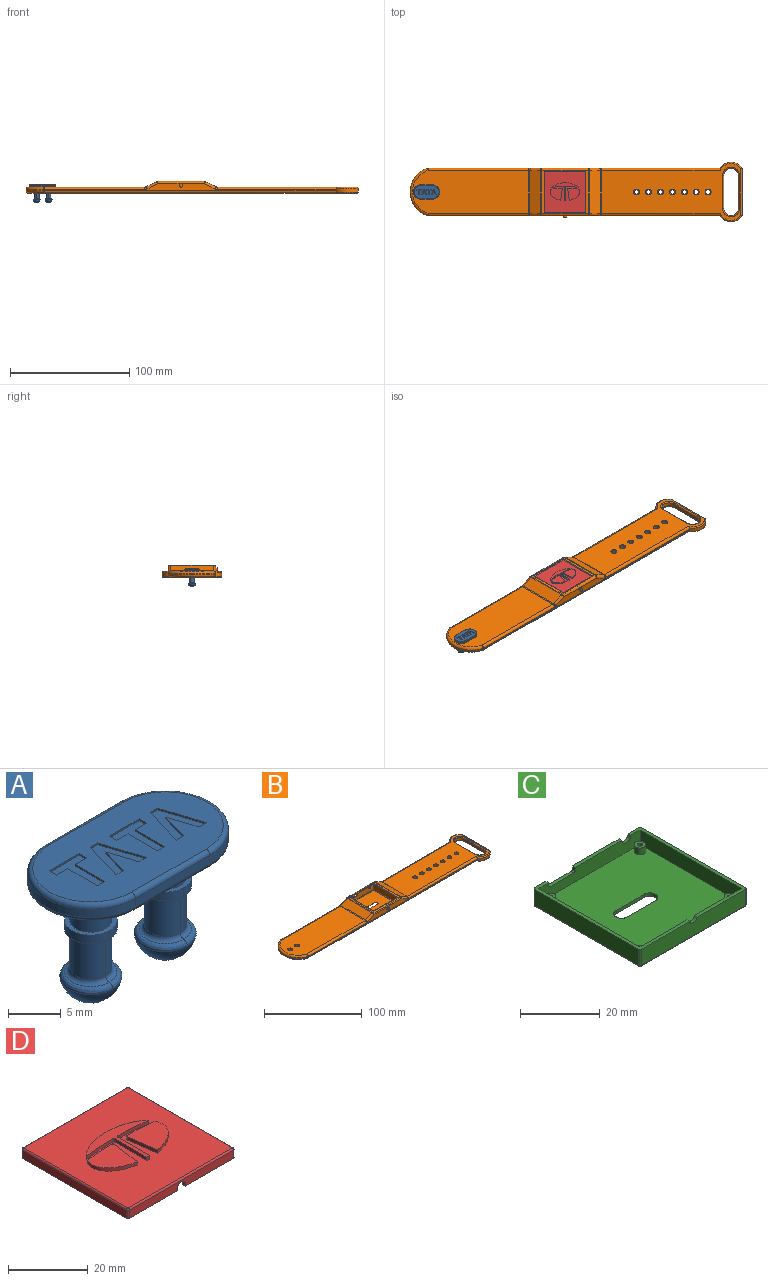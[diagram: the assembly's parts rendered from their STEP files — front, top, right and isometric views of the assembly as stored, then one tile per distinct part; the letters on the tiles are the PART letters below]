
ASSEMBLY  parts=4 mates=3
PART A: 73 faces, bbox 23x13x15 mm
  f0: plane 21x11mm, normal (0,0,1), area 171.1mm2, adj f16,f17,f18,f19,f38,f39,f40,f41
  f1: cylinder r=2.5mm len=5mm, axis (0,0,1), area 7.9mm2, adj f14,f15,f28
  f2: cylinder r=2mm len=4.5mm, axis (0,0,1), area 28.4mm2, adj f12,f27,f32
  f3: cylinder r=2mm len=4.5mm, axis (0,0,1), area 28.4mm2, adj f14,f25,f30
  f4: plane 10x1mm, normal (0,1,0), area 10mm2, adj f5,f7,f16,f20
  f5: cylinder r=6mm len=12mm, axis (0,0,1), area 18.8mm2, adj f4,f6,f17,f21
  f6: plane 10x1mm, normal (0,-1,0), area 10mm2, adj f5,f7,f19,f23
  f7: cylinder r=6mm len=12mm, axis (0,0,1), area 18.8mm2, adj f4,f6,f18,f22
  f8: plane 21x11mm, normal (0,0,-1), area 179.9mm2, adj f9,f10,f20,f21,f22,f23
  f9: cylinder r=2mm len=4mm, axis (0,0,1), area 50.3mm2, adj f8,f13
  f10: cylinder r=2mm len=4mm, axis (0,0,1), area 50.3mm2, adj f8,f15
  f11: cylinder r=2.5mm len=5mm, axis (0,0,1), area 7.9mm2, adj f12,f13,f29
  f12: plane 5.02x5mm, normal (0,0,-1), area 7mm2, adj f2,f11,f27,f29
  f13: plane 5.02x5mm, normal (0,0,1), area 7.1mm2, adj f9,f11,f29
  f14: plane 5.02x5mm, normal (0,0,-1), area 7mm2, adj f1,f3,f25,f28
  f15: plane 5.02x5mm, normal (0,0,1), area 7.1mm2, adj f1,f10,f28
  f16: cylinder r=0.5mm len=10mm, axis (-1,0,0), area 7.9mm2, adj f0,f4,f17,f18
  f17: torus R=5.5mm, axis (0,0,1), area 14.4mm2, adj f0,f5,f16,f19
  f18: torus R=5.5mm, axis (0,0,1), area 14.4mm2, adj f0,f7,f16,f19
  f19: cylinder r=0.5mm len=10mm, axis (1,0,0), area 7.9mm2, adj f0,f6,f17,f18
  f20: cylinder r=0.5mm len=10mm, axis (1,0,0), area 7.9mm2, adj f4,f8,f21,f22
  f21: torus R=5.5mm, axis (0,0,1), area 14.4mm2, adj f5,f8,f20,f23
  f22: torus R=5.5mm, axis (0,0,1), area 14.4mm2, adj f7,f8,f20,f23
  f23: cylinder r=0.5mm len=10mm, axis (-1,0,0), area 7.9mm2, adj f6,f8,f21,f22
  f24: sphere r=3mm, area 0mm2, adj f36,f37
  f25: cylinder r=2mm len=4.5mm, axis (0,0,1), area 28.4mm2, adj f3,f14,f31
  f26: sphere r=3mm, area 113.1mm2, adj f34,f35
  f27: cylinder r=2mm len=4.5mm, axis (0,0,1), area 28.4mm2, adj f2,f12,f33
  f28: cylinder r=2.5mm len=5mm, axis (0,0,1), area 7.9mm2, adj f1,f14,f15
  f29: cylinder r=2.5mm len=5mm, axis (0,0,1), area 7.9mm2, adj f11,f12,f13
  f30: torus R=2.5mm, axis (0,0,1), area 5.1mm2, adj f3,f31,f37
  f31: torus R=2.5mm, axis (0,0,1), area 5.2mm2, adj f25,f30,f36
  f32: torus R=2.5mm, axis (0,0,1), area 5.2mm2, adj f2,f33,f34
  f33: torus R=2.5mm, axis (0,0,1), area 5.1mm2, adj f27,f32,f35
  f34: bspline ~6.12x3.71mm, area 7.6mm2, adj f26,f32,f35
  f35: bspline ~5.89x2.93mm, area 7.5mm2, adj f26,f33,f34
  f36: bspline ~6.12x3.71mm, area 7.6mm2, adj f24,f31,f37
  f37: bspline ~5.89x2.93mm, area 7.5mm2, adj f24,f30,f36
  f38: plane 3.96x0.2mm, normal (-1,0,0), area 0.8mm2, adj f0,f39,f45,f46
  f39: plane 1.5x0.2mm, normal (0,1,0), area 0.3mm2, adj f0,f38,f40,f46
  f40: plane 1x0.2mm, normal (-1,0,0), area 0.2mm2, adj f0,f39,f41,f46
  f41: plane 4x0.2mm, normal (0,-1,0), area 0.8mm2, adj f0,f40,f42,f46
  f42: plane 1x0.2mm, normal (1,0,0), area 0.2mm2, adj f0,f41,f43,f46
  f43: plane 1.5x0.2mm, normal (0,1,0), area 0.3mm2, adj f0,f42,f44,f46
  f44: plane 3.96x0.2mm, normal (1,0,0), area 0.8mm2, adj f0,f43,f45,f46
  f45: plane 1x0.2mm, normal (0,1,0), area 0.2mm2, adj f0,f38,f44,f46
  f46: plane 4.96x4mm, normal (0,0,1), area 8mm2, adj f38,f39,f40,f41,f42,f43,f44,f45
  f47: plane 1x0.2mm, normal (0,-1,0), area 0.2mm2, adj f0,f48,f53,f54
  f48: plane 4.96x1.5mm, normal (0.96,-0.29,0), area 1mm2, adj f0,f47,f49,f54
  f49: plane 0.98x0.2mm, normal (-0.01,1,0), area 0.2mm2, adj f0,f48,f50,f54
  f50: plane 3.37x1.02mm, normal (-0.96,0.29,0), area 0.7mm2, adj f0,f49,f51,f54
  f51: plane 3.38x1.08mm, normal (0.95,0.3,0), area 0.7mm2, adj f0,f50,f52,f54
  f52: plane 1x0.2mm, normal (0,1,0), area 0.2mm2, adj f0,f51,f53,f54
  f53: plane 4.96x1.58mm, normal (-0.95,-0.3,0), area 1mm2, adj f0,f47,f52,f54
  f54: plane 4.96x4.08mm, normal (0,0,1), area 9mm2, adj f47,f48,f49,f50,f51,f52,f53
  f55: plane 3.37x1.02mm, normal (-0.96,0.29,0), area 0.7mm2, adj f0,f56,f62,f63
  f56: plane 3.38x1.08mm, normal (0.95,0.3,0), area 0.7mm2, adj f0,f55,f57,f63
  f57: plane 1x0.2mm, normal (0,1,0), area 0.2mm2, adj f0,f56,f58,f63
  f58: plane 0.2x0.01mm, normal (-1,0,0), area 0mm2, adj f0,f57,f59,f63
  f59: plane 4.94x1.57mm, normal (-0.95,-0.3,0), area 1mm2, adj f0,f58,f60,f63
  f60: plane 1x0.2mm, normal (0,-1,0), area 0.2mm2, adj f0,f59,f61,f63
  f61: plane 4.96x1.5mm, normal (0.96,-0.29,0), area 1mm2, adj f0,f60,f62,f63
  f62: plane 0.98x0.2mm, normal (-0.01,1,0), area 0.2mm2, adj f0,f55,f61,f63
  f63: plane 4.96x4.08mm, normal (0,0,1), area 9mm2, adj f55,f56,f57,f58,f59,f60,f61,f62
  f64: plane 1x0.2mm, normal (1,0,0), area 0.2mm2, adj f0,f65,f71,f72
  f65: plane 1.5x0.2mm, normal (0,1,0), area 0.3mm2, adj f0,f64,f66,f72
  f66: plane 3.96x0.2mm, normal (1,0,0), area 0.8mm2, adj f0,f65,f67,f72
  f67: plane 1x0.2mm, normal (0,1,0), area 0.2mm2, adj f0,f66,f68,f72
  f68: plane 3.96x0.2mm, normal (-1,0,0), area 0.8mm2, adj f0,f67,f69,f72
  f69: plane 1.5x0.2mm, normal (0,1,0), area 0.3mm2, adj f0,f68,f70,f72
  f70: plane 1x0.2mm, normal (-1,0,0), area 0.2mm2, adj f0,f69,f71,f72
  f71: plane 4x0.2mm, normal (0,-1,0), area 0.8mm2, adj f0,f64,f70,f72
  f72: plane 4.96x4mm, normal (0,0,1), area 8mm2, adj f64,f65,f66,f67,f68,f69,f70,f71
PART B: 146 faces, bbox 280.6x51.7x10 mm
  f0: plane 275.33x47.84mm, normal (0,0,-1), area 9165.8mm2, adj f3,f6,f45,f46,f47,f48,f49,f50
  f1: plane 244.71x6mm, normal (0,1,0), area 451.4mm2, adj f2,f3,f18,f21,f28,f29,f32,f33
  f2: cylinder r=2mm len=84.23mm, axis (-1,0,0), area 264.6mm2, adj f1,f11,f18,f140
  f3: cylinder r=2mm len=244.74mm, axis (-1,0,0), area 768.8mm2, adj f0,f1,f36,f49,f144
  f4: plane 244.71x6mm, normal (0,-1,0), area 483.1mm2, adj f5,f6,f14,f15,f19,f22,f23,f26
  f5: cylinder r=2mm len=84.23mm, axis (1,0,0), area 264.6mm2, adj f4,f11,f14,f138
  f6: cylinder r=2mm len=244.74mm, axis (1,0,0), area 768.8mm2, adj f0,f4,f35,f50,f141
  f7: plane 37x37mm, normal (0,0,1), area 1316.4mm2, adj f82,f83,f84,f85,f132,f133,f134,f135
  f8: plane 37x8mm, normal (0,-1,0), area 257.3mm2, adj f78,f82,f86,f92,f98,f99,f100,f101
  f9: plane 39.06x36mm, normal (0,0,1), area 181mm2, adj f19,f20,f27,f28,f94,f95,f96,f97
  f10: plane 36x9.16mm, normal (-0.45,0,0.89), area 368.5mm2, adj f15,f16,f20,f21
  f11: plane 97.53x36mm, normal (0,0,1), area 3344.7mm2, adj f2,f5,f16,f130,f131,f137
  f12: plane 36x9.16mm, normal (0.45,0,0.89), area 368.5mm2, adj f23,f27,f30,f33
  f13: plane 116.86x47.84mm, normal (0,0,1), area 3679.7mm2, adj f22,f29,f30,f51,f52,f53,f54,f55
  f14: torus R=4mm, axis (0,1,0), area 4mm2, adj f4,f5,f15,f16
  f15: cylinder r=2mm len=10.05mm, axis (-0.89,0,-0.45), area 32.2mm2, adj f4,f10,f14,f17
  f16: cylinder r=2mm len=36mm, axis (0,-1,0), area 33.4mm2, adj f10,f11,f14,f18
  f17: sphere r=2mm, area 1.9mm2, adj f15,f19,f20
  f18: torus R=4mm, axis (0,1,0), area 4mm2, adj f1,f2,f16,f21
  f19: cylinder r=2mm len=39.06mm, axis (-1,0,0), area 122.7mm2, adj f4,f9,f17,f24
  f20: cylinder r=2mm len=36mm, axis (0,1,0), area 33.4mm2, adj f9,f10,f17,f25
  f21: cylinder r=2mm len=10.05mm, axis (0.89,0,0.45), area 32.2mm2, adj f1,f10,f18,f25
  f22: cylinder r=2mm len=99.57mm, axis (-1,0,0), area 312.7mm2, adj f4,f13,f26,f34,f56
  f23: cylinder r=2mm len=10.05mm, axis (0.89,0,-0.45), area 32.2mm2, adj f4,f12,f24,f26
  f24: sphere r=2mm, area 1.9mm2, adj f19,f23,f27
  f25: sphere r=2mm, area 1.9mm2, adj f20,f21,f28
  f26: torus R=4mm, axis (0,1,0), area 4mm2, adj f4,f22,f23,f30
  f27: cylinder r=2mm len=36mm, axis (0,1,0), area 33.4mm2, adj f9,f12,f24,f31
  f28: cylinder r=2mm len=39.06mm, axis (1,0,0), area 122.7mm2, adj f1,f9,f25,f31,f98
  f29: cylinder r=2mm len=99.57mm, axis (1,0,0), area 312.7mm2, adj f1,f13,f32,f40,f55
  f30: cylinder r=2mm len=36mm, axis (0,-1,0), area 33.4mm2, adj f12,f13,f26,f32
  f31: sphere r=2mm, area 1.9mm2, adj f27,f28,f33
  f32: torus R=4mm, axis (0,1,0), area 4mm2, adj f1,f29,f30,f33
  f33: cylinder r=2mm len=10.05mm, axis (-0.89,0,0.45), area 32.2mm2, adj f1,f12,f31,f32
  f34: plane 2x1.89mm, normal (-1,0,0), area 0.4mm2, adj f22,f41,f56
  f35: plane 2x1.89mm, normal (-1,0,0), area 0.4mm2, adj f6,f41,f50
  f36: plane 2x1.89mm, normal (-1,0,0), area 0.4mm2, adj f3,f43,f49
  f37: cylinder r=6mm len=12mm, axis (0,0,-1), area 56.5mm2, adj f38,f44,f45,f51
  f38: plane 27.84x3mm, normal (1,0,0), area 83.5mm2, adj f37,f39,f46,f52
  f39: cylinder r=6mm len=12mm, axis (0,0,-1), area 56.5mm2, adj f38,f44,f48,f54
  f40: plane 2x1.89mm, normal (-1,0,0), area 0.4mm2, adj f29,f43,f55
  f41: cylinder r=11mm len=18.15mm, axis (0,0,-1), area 64mm2, adj f4,f34,f35,f50,f56,f117
  f42: plane 39.38x3mm, normal (1,0,0), area 118.1mm2, adj f117,f118,f121,f122
  f43: cylinder r=11mm len=18.15mm, axis (0,0,-1), area 64mm2, adj f1,f36,f40,f49,f55,f122
  f44: plane 27.84x3mm, normal (-1,0,0), area 83.5mm2, adj f37,f39,f47,f53
  f45: torus R=7mm, axis (0,0,1), area 31.4mm2, adj f0,f37,f46,f47
  f46: cylinder r=1mm len=27.84mm, axis (0,1,0), area 43.7mm2, adj f0,f38,f45,f48
  f47: cylinder r=1mm len=27.84mm, axis (0,-1,0), area 43.7mm2, adj f0,f44,f45,f48
  f48: torus R=7mm, axis (0,0,1), area 31.4mm2, adj f0,f39,f46,f47
  f49: torus R=10mm, axis (0,0,1), area 33.4mm2, adj f0,f3,f36,f43,f123
  f50: torus R=10mm, axis (0,0,1), area 33.4mm2, adj f0,f6,f35,f41,f119
  f51: torus R=7mm, axis (0,0,-1), area 31.4mm2, adj f13,f37,f52,f53
  f52: cylinder r=1mm len=27.84mm, axis (0,1,0), area 43.7mm2, adj f13,f38,f51,f54
  f53: cylinder r=1mm len=27.84mm, axis (0,-1,0), area 43.7mm2, adj f13,f44,f51,f54
  f54: torus R=7mm, axis (0,0,-1), area 31.4mm2, adj f13,f39,f52,f53
  f55: torus R=10mm, axis (0,0,-1), area 33.4mm2, adj f13,f29,f40,f43,f120
  f56: torus R=10mm, axis (0,0,-1), area 33.4mm2, adj f13,f22,f34,f41,f116
  f57: cylinder r=2mm len=4mm, axis (0,0,-1), area 50.3mm2, adj f64,f65
  f58: cylinder r=2mm len=4mm, axis (0,0,-1), area 50.3mm2, adj f66,f67
  f59: cylinder r=2mm len=4mm, axis (0,0,-1), area 50.3mm2, adj f68,f69
  f60: cylinder r=2mm len=4mm, axis (0,0,-1), area 50.3mm2, adj f70,f71
  f61: cylinder r=2mm len=4mm, axis (0,0,-1), area 50.3mm2, adj f72,f73
  f62: cylinder r=2mm len=4mm, axis (0,0,-1), area 50.3mm2, adj f74,f75
  f63: cylinder r=2mm len=4mm, axis (0,0,-1), area 50.3mm2, adj f76,f77
  f64: torus R=2.5mm, axis (0,0,1), area 10.8mm2, adj f0,f57
  f65: torus R=2.5mm, axis (0,0,-1), area 10.8mm2, adj f13,f57
  f66: torus R=2.5mm, axis (0,0,1), area 10.8mm2, adj f0,f58
  f67: torus R=2.5mm, axis (0,0,-1), area 10.8mm2, adj f13,f58
  f68: torus R=2.5mm, axis (0,0,1), area 10.8mm2, adj f0,f59
  f69: torus R=2.5mm, axis (0,0,-1), area 10.8mm2, adj f13,f59
  f70: torus R=2.5mm, axis (0,0,1), area 10.8mm2, adj f0,f60
  f71: torus R=2.5mm, axis (0,0,-1), area 10.8mm2, adj f13,f60
  f72: torus R=2.5mm, axis (0,0,1), area 10.8mm2, adj f0,f61
  f73: torus R=2.5mm, axis (0,0,-1), area 10.8mm2, adj f13,f61
  f74: torus R=2.5mm, axis (0,0,1), area 10.8mm2, adj f0,f62
  f75: torus R=2.5mm, axis (0,0,-1), area 10.8mm2, adj f13,f62
  f76: torus R=2.5mm, axis (0,0,1), area 10.8mm2, adj f0,f63
  f77: torus R=2.5mm, axis (0,0,-1), area 10.8mm2, adj f13,f63
  f78: plane 38x38mm, normal (0,0,-1), area 218.8mm2, adj f8,f79,f80,f81,f86,f88,f90,f92
  f79: plane 37x8mm, normal (-1,0,0), area 296mm2, adj f78,f84,f90,f92
  f80: plane 37x8mm, normal (1,0,0), area 296mm2, adj f78,f83,f86,f88
  f81: plane 37x8mm, normal (0,1,0), area 291.1mm2, adj f78,f85,f88,f90,f114
  f82: cylinder r=0.5mm len=37mm, axis (-1,0,0), area 29.1mm2, adj f7,f8,f87,f93
  f83: cylinder r=0.5mm len=37mm, axis (0,1,0), area 29.1mm2, adj f7,f80,f87,f89
  f84: cylinder r=0.5mm len=37mm, axis (0,1,0), area 29.1mm2, adj f7,f79,f91,f93
  f85: cylinder r=0.5mm len=37mm, axis (-1,0,0), area 29.1mm2, adj f7,f81,f89,f91
  f86: cylinder r=0.5mm len=8mm, axis (0,0,1), area 6.3mm2, adj f8,f78,f80,f87
  f87: sphere r=0.5mm, area 0.4mm2, adj f82,f83,f86
  f88: cylinder r=0.5mm len=8mm, axis (0,0,1), area 6.3mm2, adj f78,f80,f81,f89
  f89: sphere r=0.5mm, area 0.4mm2, adj f83,f85,f88
  f90: cylinder r=0.5mm len=8mm, axis (0,0,1), area 6.3mm2, adj f78,f79,f81,f91
  f91: sphere r=0.5mm, area 0.4mm2, adj f84,f85,f90
  f92: cylinder r=0.5mm len=8mm, axis (0,0,1), area 6.3mm2, adj f8,f78,f79,f93
  f93: sphere r=0.5mm, area 0.4mm2, adj f82,f84,f92
  f94: cylinder r=0.5mm len=35mm, axis (1,0,0), area 54mm2, adj f9,f78,f95,f96
  f95: cylinder r=0.5mm len=35mm, axis (0,1,0), area 54mm2, adj f9,f78,f94,f97
  f96: cylinder r=0.5mm len=35mm, axis (0,-1,0), area 54mm2, adj f9,f78,f94,f97
  f97: cylinder r=0.5mm len=35mm, axis (-1,0,0), area 54mm2, adj f9,f78,f95,f96
  f98: plane 7.21x1mm, normal (0,0,-1), area 7.2mm2, adj f8,f28,f99,f109
  f99: cylinder r=0.5mm len=1mm, axis (0,1,0), area 0.2mm2, adj f1,f8,f98,f100
  f100: plane 1.63x1mm, normal (-0.87,0,-0.5), area 1.9mm2, adj f1,f8,f99,f101
  f101: cylinder r=0.5mm len=1mm, axis (0,1,0), area 0.3mm2, adj f1,f8,f100,f102
  f102: plane 1x0.9mm, normal (-1,0,0), area 0.9mm2, adj f1,f8,f101,f103
  f103: cylinder r=0.5mm len=1mm, axis (0,1,0), area 0.8mm2, adj f1,f8,f102,f104
  f104: plane 8.5x1mm, normal (0,0,1), area 8.5mm2, adj f1,f8,f103,f105
  f105: cylinder r=0.5mm len=1mm, axis (0,1,0), area 0.8mm2, adj f1,f8,f104,f106
  f106: plane 1x0.9mm, normal (1,0,0), area 0.9mm2, adj f1,f8,f105,f107
  f107: cylinder r=0.5mm len=1mm, axis (0,1,0), area 0.3mm2, adj f1,f8,f106,f108
  f108: plane 1.63x1mm, normal (0.87,0,-0.5), area 1.9mm2, adj f1,f8,f107,f109
  f109: cylinder r=0.5mm len=1mm, axis (0,1,0), area 0.2mm2, adj f1,f8,f98,f108
  f110: cylinder r=1.62mm len=3.25mm, axis (0,1,0), area 10.2mm2, adj f1,f8
  f111: cylinder r=1.5mm len=3mm, axis (0,1,0), area 14.1mm2, adj f4,f112
  f112: plane 3x3mm, normal (0,-1,0), area 7.1mm2, adj f111
  f113: cylinder r=0.75mm len=2.5mm, axis (0,1,0), area 11.8mm2, adj f115,f145
  f114: cylinder r=1.25mm len=2.5mm, axis (0,1,0), area 15.7mm2, adj f81,f115
  f115: plane 2.5x2.5mm, normal (0,1,0), area 3.1mm2, adj f113,f114
  f116: sphere r=1mm, area 0.6mm2, adj f56,f117,f118
  f117: cylinder r=1mm len=3mm, axis (0,0,-1), area 1.8mm2, adj f41,f42,f116,f119
  f118: cylinder r=1mm len=39.38mm, axis (0,1,0), area 61.9mm2, adj f13,f42,f116,f120
  f119: sphere r=1mm, area 0.6mm2, adj f50,f117,f121
  f120: sphere r=1mm, area 0.6mm2, adj f55,f118,f122
  f121: cylinder r=1mm len=39.38mm, axis (0,1,0), area 61.9mm2, adj f0,f42,f119,f123
  f122: cylinder r=1mm len=3mm, axis (0,0,-1), area 1.8mm2, adj f42,f43,f120,f123
  f123: sphere r=1mm, area 0.6mm2, adj f49,f121,f122
  f124: cylinder r=2.5mm len=5mm, axis (0,0,-1), area 15.7mm2, adj f0,f125
  f125: plane 5x5mm, normal (0,0,-1), area 7.1mm2, adj f124,f128
  f126: cylinder r=2.5mm len=5mm, axis (0,0,-1), area 15.7mm2, adj f0,f127
  f127: plane 5x5mm, normal (0,0,-1), area 7.1mm2, adj f126,f129
  f128: cylinder r=2mm len=4mm, axis (0,0,1), area 44mm2, adj f125,f130
  f129: cylinder r=2mm len=4mm, axis (0,0,1), area 44mm2, adj f127,f131
  f130: torus R=2.5mm, axis (0,0,-1), area 10.8mm2, adj f11,f128
  f131: torus R=2.5mm, axis (0,0,-1), area 10.8mm2, adj f11,f129
  f132: plane 10x0.5mm, normal (0,-1,0), area 5mm2, adj f0,f7,f133,f135
  f133: cylinder r=2mm len=4mm, axis (0,0,-1), area 3.1mm2, adj f0,f7,f132,f134
  f134: plane 10x0.5mm, normal (0,1,0), area 5mm2, adj f0,f7,f133,f135
  f135: cylinder r=2mm len=4mm, axis (0,0,-1), area 3.1mm2, adj f0,f7,f132,f134
  f136: cylinder r=20.83mm len=39.82mm, axis (0,0,1), area 53mm2, adj f137,f139,f142,f143
  f137: torus R=18.83mm, axis (0,0,-1), area 160.7mm2, adj f11,f136,f138,f140
  f138: sphere r=2mm, area 1.2mm2, adj f5,f137,f139
  f139: cylinder r=2mm len=1mm, axis (0,0,1), area 0.6mm2, adj f4,f136,f138,f141
  f140: sphere r=2mm, area 1.2mm2, adj f2,f137,f142
  f141: sphere r=2mm, area 1.2mm2, adj f6,f139,f143
  f142: cylinder r=2mm len=1mm, axis (0,0,1), area 0.6mm2, adj f1,f136,f140,f144
  f143: torus R=18.83mm, axis (0,0,1), area 160.7mm2, adj f0,f136,f141,f144
  f144: sphere r=2mm, area 1.2mm2, adj f3,f142,f143
  f145: plane 1.5x1.5mm, normal (0,1,0), area 1.8mm2, adj f113
PART C: 98 faces, bbox 38.3x38.3x5.8 mm
  f0: plane 3.29x3.29mm, normal (0,0,-1), area 6.8mm2, adj f68,f78,f79,f80,f81,f95,f96
  f1: cylinder r=0.65mm len=1.3mm, axis (0,0,1), area 3.1mm2, adj f4,f56,f92,f94
  f2: cylinder r=0.65mm len=1.3mm, axis (0,0,1), area 0.2mm2, adj f3,f5,f92,f93
  f3: cylinder r=0.65mm len=1.3mm, axis (0,0,1), area 0.2mm2, adj f2,f4,f92,f93
  f4: cylinder r=0.65mm len=1.3mm, axis (0,0,1), area 0.2mm2, adj f1,f3,f92,f93
  f5: cylinder r=0.65mm len=0.31mm, axis (0,0,1), area 0mm2, adj f2,f6,f93
  f6: plane 3.29x3.29mm, normal (0,0,-1), area 6.8mm2, adj f5,f74,f75,f76,f77,f92,f93
  f7: cylinder r=0.65mm len=1.3mm, axis (0,0,1), area 3.1mm2, adj f10,f58,f89,f91
  f8: cylinder r=0.65mm len=1.3mm, axis (0,0,1), area 0.2mm2, adj f9,f11,f89,f90
  f9: cylinder r=0.65mm len=1.3mm, axis (0,0,1), area 0.2mm2, adj f8,f10,f89,f90
  f10: cylinder r=0.65mm len=1.3mm, axis (0,0,1), area 0.2mm2, adj f7,f9,f89,f90
  f11: cylinder r=0.65mm len=0.31mm, axis (0,0,1), area 0mm2, adj f8,f12,f90
  f12: plane 3.29x3.29mm, normal (0,0,-1), area 6.8mm2, adj f11,f70,f71,f72,f73,f89,f90
  f13: plane 3.29x3.29mm, normal (0,0,-1), area 6.8mm2, adj f63,f82,f83,f84,f85,f86,f87
  f14: plane 37x37mm, normal (0,0,-1), area 1280.4mm2, adj f32,f33,f36,f37,f39,f40,f41,f42
  f15: plane 38x17.59mm, normal (0,0,1), area 57.7mm2, adj f16,f17,f20,f21,f24,f26,f28,f29
  f16: plane 37x5mm, normal (0,-1,0), area 182.9mm2, adj f15,f19,f27,f28,f33,f69
  f17: plane 36x4.5mm, normal (0,1,0), area 159.9mm2, adj f15,f19,f22,f25,f26,f69
  f18: plane 16.54x1mm, normal (0,0,1), area 16.5mm2, adj f20,f21,f44,f50
  f19: plane 38x17.59mm, normal (0,0,1), area 58mm2, adj f16,f17,f20,f21,f23,f25,f27,f30
  f20: plane 37x5mm, normal (0,1,0), area 167.8mm2, adj f15,f18,f19,f29,f30,f36,f43,f44
  f21: plane 36x4.5mm, normal (0,-1,0), area 144.8mm2, adj f15,f18,f19,f22,f25,f26,f43,f44
  f22: plane 36x36mm, normal (0,0,1), area 1215.2mm2, adj f17,f21,f25,f26,f39,f40,f41,f42
  f23: plane 37x5mm, normal (-1,0,0), area 185mm2, adj f19,f27,f30,f32
  f24: plane 37x5mm, normal (1,0,0), area 185mm2, adj f15,f28,f29,f37
  f25: plane 36x4.5mm, normal (1,0,0), area 162mm2, adj f17,f19,f21,f22
  f26: plane 36x4.5mm, normal (-1,0,0), area 162mm2, adj f15,f17,f21,f22
  f27: cylinder r=0.5mm len=5mm, axis (0,0,-1), area 3.9mm2, adj f16,f19,f23,f31
  f28: cylinder r=0.5mm len=5mm, axis (0,0,1), area 3.9mm2, adj f15,f16,f24,f35
  f29: cylinder r=0.5mm len=5mm, axis (0,0,-1), area 3.9mm2, adj f15,f20,f24,f38
  f30: cylinder r=0.5mm len=5mm, axis (0,0,1), area 3.9mm2, adj f19,f20,f23,f34
  f31: sphere r=0.5mm, area 0.4mm2, adj f27,f32,f33
  f32: cylinder r=0.5mm len=37mm, axis (0,-1,0), area 29.1mm2, adj f14,f23,f31,f34
  f33: cylinder r=0.5mm len=37mm, axis (1,0,0), area 29.1mm2, adj f14,f16,f31,f35
  f34: sphere r=0.5mm, area 0.5mm2, adj f30,f32,f36
  f35: sphere r=0.5mm, area 0.4mm2, adj f28,f33,f37
  f36: cylinder r=0.5mm len=37mm, axis (-1,0,0), area 29.1mm2, adj f14,f20,f34,f38
  f37: cylinder r=0.5mm len=37mm, axis (0,1,0), area 29.1mm2, adj f14,f24,f35,f38
  f38: sphere r=0.5mm, area 0.2mm2, adj f29,f36,f37
  f39: plane 10x1mm, normal (0,-1,0), area 10mm2, adj f14,f22,f40,f42
  f40: cylinder r=2mm len=4mm, axis (0,0,-1), area 6.3mm2, adj f14,f22,f39,f41
  f41: plane 10x1mm, normal (0,1,0), area 10mm2, adj f14,f22,f40,f42
  f42: cylinder r=2mm len=4mm, axis (0,0,-1), area 6.3mm2, adj f14,f22,f39,f41
  f43: cylinder r=0.5mm len=1mm, axis (0,1,0), area 0mm2, adj f19,f20,f21,f49
  f44: cylinder r=0.5mm len=1mm, axis (0,1,0), area 0mm2, adj f18,f20,f21,f45
  f45: plane 1x0.9mm, normal (-1,0,0), area 0.9mm2, adj f20,f21,f44,f46
  f46: cylinder r=0.5mm len=1mm, axis (0,1,0), area 0.8mm2, adj f20,f21,f45,f47
  f47: plane 8.5x1mm, normal (0,0,1), area 8.5mm2, adj f20,f21,f46,f48
  f48: cylinder r=0.5mm len=1mm, axis (0,1,0), area 0.8mm2, adj f20,f21,f47,f49
  f49: plane 1x0.9mm, normal (1,0,0), area 0.9mm2, adj f20,f21,f43,f48
  f50: cylinder r=1.62mm len=3.24mm, axis (0,1,0), area 4.8mm2, adj f15,f18,f20,f21
  f51: cylinder r=1.5mm len=3mm, axis (0,0,-1), area 18.8mm2, adj f22,f52
  f52: plane 3x3mm, normal (0,0,1), area 5.7mm2, adj f51,f67
  f53: cylinder r=1.5mm len=3mm, axis (0,0,-1), area 18.8mm2, adj f22,f54
  f54: plane 3x3mm, normal (0,0,1), area 5.7mm2, adj f53,f62
  f55: cylinder r=1.5mm len=3mm, axis (0,0,-1), area 18.8mm2, adj f22,f56
  f56: plane 3x3mm, normal (0,0,1), area 5.7mm2, adj f1,f55
  f57: cylinder r=1.5mm len=3mm, axis (0,0,-1), area 18.8mm2, adj f22,f58
  f58: plane 3x3mm, normal (0,0,1), area 5.7mm2, adj f7,f57
  f59: cylinder r=0.65mm len=1.3mm, axis (0,0,1), area 0.2mm2, adj f60,f63,f86,f87
  f60: cylinder r=0.65mm len=1.3mm, axis (0,0,1), area 0.2mm2, adj f59,f61,f86,f87
  f61: cylinder r=0.65mm len=1.3mm, axis (0,0,1), area 0.2mm2, adj f60,f62,f86,f87
  f62: cylinder r=0.65mm len=1.3mm, axis (0,0,1), area 3.1mm2, adj f54,f61,f86,f88
  f63: cylinder r=0.65mm len=0.31mm, axis (0,0,1), area 0mm2, adj f13,f59,f87
  f64: cylinder r=0.65mm len=1.3mm, axis (0,0,1), area 0.2mm2, adj f65,f68,f95,f96
  f65: cylinder r=0.65mm len=1.3mm, axis (0,0,1), area 0.2mm2, adj f64,f66,f95,f96
  f66: cylinder r=0.65mm len=1.3mm, axis (0,0,1), area 0.2mm2, adj f65,f67,f95,f96
  f67: cylinder r=0.65mm len=1.3mm, axis (0,0,1), area 3.1mm2, adj f52,f66,f95,f97
  f68: cylinder r=0.65mm len=0.31mm, axis (0,0,1), area 0mm2, adj f0,f64,f96
  f69: cylinder r=1.5mm len=2.83mm, axis (0,-1,0), area 3.7mm2, adj f15,f16,f17,f19
  f70: plane 3x0.5mm, normal (0,-1,0), area 1.5mm2, adj f12,f14,f71,f73
  f71: plane 3x0.5mm, normal (1,0,0), area 1.5mm2, adj f12,f14,f70,f72
  f72: plane 3x0.5mm, normal (0,1,0), area 1.5mm2, adj f12,f14,f71,f73
  f73: plane 3x0.5mm, normal (-1,0,0), area 1.5mm2, adj f12,f14,f70,f72
  f74: plane 3x0.5mm, normal (0,-1,0), area 1.5mm2, adj f6,f14,f75,f77
  f75: plane 3x0.5mm, normal (1,0,0), area 1.5mm2, adj f6,f14,f74,f76
  f76: plane 3x0.5mm, normal (0,1,0), area 1.5mm2, adj f6,f14,f75,f77
  f77: plane 3x0.5mm, normal (-1,0,0), area 1.5mm2, adj f6,f14,f74,f76
  f78: plane 3x0.5mm, normal (1,0,0), area 1.5mm2, adj f0,f14,f79,f81
  f79: plane 3x0.5mm, normal (0,1,0), area 1.5mm2, adj f0,f14,f78,f80
  f80: plane 3x0.5mm, normal (-1,0,0), area 1.5mm2, adj f0,f14,f79,f81
  f81: plane 3x0.5mm, normal (0,-1,0), area 1.5mm2, adj f0,f14,f78,f80
  f82: plane 3x0.5mm, normal (1,0,0), area 1.5mm2, adj f13,f14,f83,f85
  f83: plane 3x0.5mm, normal (0,1,0), area 1.5mm2, adj f13,f14,f82,f84
  f84: plane 3x0.5mm, normal (-1,0,0), area 1.5mm2, adj f13,f14,f83,f85
  f85: plane 3x0.5mm, normal (0,-1,0), area 1.5mm2, adj f13,f14,f82,f84
  f86: bspline ~2.42x2.31mm, area 9.2mm2, adj f13,f59,f60,f61,f62,f87,f88
  f87: bspline ~2.42x2.1mm, area 8.2mm2, adj f13,f59,f60,f61,f63,f86,f88
  f88: plane 0.46x0.4mm, normal (0,-1,0), area 0.1mm2, adj f62,f86,f87
  f89: bspline ~2.42x2.31mm, area 9.2mm2, adj f7,f8,f9,f10,f12,f90,f91
  f90: bspline ~2.42x2.1mm, area 8.2mm2, adj f8,f9,f10,f11,f12,f89,f91
  f91: plane 0.46x0.4mm, normal (0,-1,0), area 0.1mm2, adj f7,f89,f90
  f92: bspline ~2.42x2.31mm, area 9.2mm2, adj f1,f2,f3,f4,f6,f93,f94
  f93: bspline ~2.42x2.1mm, area 8.2mm2, adj f2,f3,f4,f5,f6,f92,f94
  f94: plane 0.46x0.4mm, normal (0,-1,0), area 0.1mm2, adj f1,f92,f93
  f95: bspline ~2.42x2.31mm, area 9.2mm2, adj f0,f64,f65,f66,f67,f96,f97
  f96: bspline ~2.42x2.1mm, area 8.2mm2, adj f0,f64,f65,f66,f68,f95,f97
  f97: plane 0.46x0.4mm, normal (0,-1,0), area 0.1mm2, adj f67,f95,f96
PART D: 104 faces, bbox 41x41x9 mm
  f0: plane 3.3x3.3mm, normal (0,0,-1), area 2.5mm2, adj f1,f6,f7,f8,f9
  f1: bspline ~2.73x2.65mm, area 12.8mm2, adj f0,f2,f3,f4,f5,f6,f8
  f2: cylinder r=0.75mm len=1.5mm, axis (0,0,-1), area 0.2mm2, adj f1,f3,f6,f8
  f3: cylinder r=0.75mm len=1.5mm, axis (0,0,-1), area 0.2mm2, adj f1,f2,f4,f8
  f4: cylinder r=0.75mm len=1.5mm, axis (0,0,-1), area 0.2mm2, adj f1,f3,f8
  f5: plane 0.46x0.4mm, normal (0,-1,0), area 0.1mm2, adj f1,f8
  f6: cylinder r=0.75mm len=1.5mm, axis (0,0,-1), area 0.2mm2, adj f0,f1,f2,f8
  f7: cylinder r=0.75mm len=2.5mm, axis (0,0,-1), area 5.9mm2, adj f0
  f8: bspline ~2.65x2.48mm, area 11.7mm2, adj f0,f1,f2,f3,f4,f5,f6
  f9: cylinder r=1.5mm len=3.5mm, axis (0,0,1), area 33mm2, adj f0,f10
  f10: plane 36x36mm, normal (0,0,-1), area 1267.7mm2, adj f9,f11,f60,f61,f62,f63,f64,f65
  f11: plane 36x2mm, normal (1,0,0), area 72mm2, adj f10,f12,f60,f65
  f12: plane 38x17.59mm, normal (0,0,-1), area 58mm2, adj f11,f13,f54,f55,f56,f57,f58,f59
  f13: cylinder r=0.5mm len=1mm, axis (0,1,0), area 0.2mm2, adj f12,f14,f54,f65
  f14: plane 1.63x1mm, normal (0.87,0,-0.5), area 1.9mm2, adj f13,f15,f54,f65
  f15: cylinder r=0.5mm len=1mm, axis (0,1,0), area 0.5mm2, adj f14,f16,f54,f64,f65
  f16: plane 6.61x1mm, normal (0,0,-1), area 6.6mm2, adj f15,f17,f54,f64
  f17: cylinder r=0.5mm len=1mm, axis (0,1,0), area 0.5mm2, adj f16,f18,f54,f63,f64
  f18: plane 1.63x1mm, normal (-0.87,0,-0.5), area 1.9mm2, adj f17,f19,f54,f63
  f19: cylinder r=0.5mm len=1mm, axis (0,1,0), area 0.2mm2, adj f18,f20,f54,f63
  f20: plane 16.54x1mm, normal (0,0,-1), area 16.5mm2, adj f19,f21,f54,f63
  f21: cylinder r=1.62mm len=3.25mm, axis (0,1,0), area 5.4mm2, adj f20,f22,f54,f63
  f22: plane 38x17.59mm, normal (0,0,-1), area 57.7mm2, adj f21,f23,f52,f53,f54,f58,f59,f61
  f23: cylinder r=0.5mm len=2.5mm, axis (0,0,-1), area 2mm2, adj f22,f24,f52,f58
  f24: sphere r=0.5mm, area 0.4mm2, adj f23,f25,f51
  f25: cylinder r=0.5mm len=37mm, axis (0,1,0), area 29.1mm2, adj f24,f26,f50,f52
  f26: plane 37x37mm, normal (0,0,1), area 1155.4mm2, adj f25,f27,f29,f30,f31,f32,f34,f35
  f27: cylinder r=0.5mm len=1mm, axis (0,0,-1), area 0.8mm2, adj f26,f28,f29,f31
  f28: plane 10.17x9.97mm, normal (0,0,1), area 75.5mm2, adj f27,f29,f30,f31
  f29: plane 9.42x1.3mm, normal (-0.99,-0.14,0), area 9.5mm2, adj f26,f27,f28,f30
  f30: extruded ~9.3x8.86mm, area 14.5mm2, adj f26,f28,f29,f31
  f31: cylinder r=64.85mm len=9.26mm, axis (0,0,-1), area 9.3mm2, adj f26,f27,f28,f30
  f32: cylinder r=0.5mm len=1mm, axis (0,0,-1), area 0.7mm2, adj f26,f33,f34,f40
  f33: plane 22.08x15mm, normal (0,0,1), area 62.6mm2, adj f32,f34,f35,f36,f37,f38,f39,f40
  f34: cylinder r=55.6mm len=10.07mm, axis (0,0,-1), area 10.1mm2, adj f26,f32,f33,f35
  f35: extruded ~22.08x3.98mm, area 24.1mm2, adj f26,f33,f34,f36
  f36: cylinder r=55.6mm len=10.07mm, axis (0,0,-1), area 10.1mm2, adj f26,f33,f35,f37
  f37: cylinder r=0.5mm len=1mm, axis (0,0,-1), area 0.7mm2, adj f26,f33,f36,f38
  f38: plane 11.27x1mm, normal (-1,0,0), area 11.3mm2, adj f26,f33,f37,f39
  f39: extruded ~1.02x1mm, area 1mm2, adj f26,f33,f38,f40
  f40: plane 11.27x1mm, normal (1,0,0), area 11.3mm2, adj f26,f32,f33,f39
  f41: cylinder r=0.5mm len=37mm, axis (-1,0,0), area 29.1mm2, adj f26,f42,f50,f54
  f42: sphere r=0.5mm, area 0.5mm2, adj f41,f43,f55
  f43: cylinder r=0.5mm len=37mm, axis (0,-1,0), area 29.1mm2, adj f26,f42,f44,f56
  f44: sphere r=0.5mm, area 0.4mm2, adj f43,f51,f57
  f45: plane 9.42x1.3mm, normal (0.99,-0.14,0), area 9.5mm2, adj f26,f46,f47,f49
  f46: plane 10.17x9.97mm, normal (0,0,1), area 75.5mm2, adj f45,f47,f48,f49
  f47: cylinder r=0.5mm len=1mm, axis (0,0,-1), area 0.8mm2, adj f26,f45,f46,f48
  f48: cylinder r=64.85mm len=9.26mm, axis (0,0,-1), area 9.3mm2, adj f26,f46,f47,f49
  f49: extruded ~9.3x8.86mm, area 14.5mm2, adj f26,f45,f46,f48
  f50: sphere r=0.5mm, area 0.4mm2, adj f25,f41,f53
  f51: cylinder r=0.5mm len=37mm, axis (1,0,0), area 29.1mm2, adj f24,f26,f44,f58
  f52: plane 37x2.5mm, normal (1,0,0), area 92.5mm2, adj f22,f23,f25,f53
  f53: cylinder r=0.5mm len=2.5mm, axis (0,0,1), area 2mm2, adj f22,f50,f52,f54
  f54: plane 37x2.5mm, normal (0,1,0), area 70.3mm2, adj f12,f13,f14,f15,f16,f17,f18,f19
  f55: cylinder r=0.5mm len=2.5mm, axis (0,0,-1), area 2mm2, adj f12,f42,f54,f56
  f56: plane 37x2.5mm, normal (-1,0,0), area 92.5mm2, adj f12,f43,f55,f57
  f57: cylinder r=0.5mm len=2.5mm, axis (0,0,1), area 2mm2, adj f12,f44,f56,f58
  f58: plane 37x2.5mm, normal (0,-1,0), area 87.5mm2, adj f12,f22,f23,f51,f57,f59
  f59: cylinder r=1.5mm len=3mm, axis (0,-1,0), area 5.7mm2, adj f12,f22,f58,f60,f61
  f60: plane 18x2mm, normal (0,1,0), area 33.5mm2, adj f10,f11,f12,f59
  f61: plane 18x2mm, normal (0,1,0), area 33.5mm2, adj f10,f22,f59,f62
  f62: plane 36x2mm, normal (-1,0,0), area 72mm2, adj f10,f22,f61,f63
  f63: plane 24.14x2mm, normal (0,-1,0), area 42.4mm2, adj f10,f17,f18,f19,f20,f21,f22,f62
  f64: plane 7.21x0.1mm, normal (0,1,0), area 0.7mm2, adj f10,f15,f16,f17
  f65: plane 4.64x2mm, normal (0,-1,0), area 8mm2, adj f10,f11,f12,f13,f14,f15
  f66: cylinder r=1.5mm len=3.5mm, axis (0,0,1), area 33mm2, adj f10,f67
  f67: plane 3.3x3.3mm, normal (0,0,-1), area 2.5mm2, adj f66,f68,f75,f76,f77
  f68: bspline ~2.73x2.65mm, area 12.8mm2, adj f67,f69,f70,f71,f72,f74,f75,f77
  f69: cylinder r=0.75mm len=1.5mm, axis (0,0,-1), area 0.2mm2, adj f68,f70,f75,f77
  f70: cylinder r=0.75mm len=1.5mm, axis (0,0,-1), area 0.2mm2, adj f68,f69,f71,f77
  f71: cylinder r=0.75mm len=1.5mm, axis (0,0,-1), area 0.2mm2, adj f68,f70,f72,f77
  f72: cylinder r=0.75mm len=1.5mm, axis (0,0,-1), area 1.4mm2, adj f68,f71,f73,f74
  f73: plane 1.5x1.5mm, normal (0,0,-1), area 1.8mm2, adj f72
  f74: plane 0.46x0.4mm, normal (0,-1,0), area 0.1mm2, adj f68,f72,f77
  f75: cylinder r=0.75mm len=1.5mm, axis (0,0,-1), area 0.2mm2, adj f67,f68,f69,f77
  f76: cylinder r=0.75mm len=2.5mm, axis (0,0,-1), area 5.9mm2, adj f67
  f77: bspline ~2.65x2.48mm, area 11.7mm2, adj f67,f68,f69,f70,f71,f74,f75
  f78: cylinder r=1.5mm len=3.5mm, axis (0,0,1), area 33mm2, adj f10,f79
  f79: plane 3.3x3.3mm, normal (0,0,-1), area 2.5mm2, adj f78,f80,f87,f88,f89
  f80: bspline ~2.73x2.65mm, area 12.8mm2, adj f79,f81,f82,f83,f84,f86,f87,f89
  f81: cylinder r=0.75mm len=1.5mm, axis (0,0,-1), area 0.2mm2, adj f80,f82,f87,f89
  f82: cylinder r=0.75mm len=1.5mm, axis (0,0,-1), area 0.2mm2, adj f80,f81,f83,f89
  f83: cylinder r=0.75mm len=1.5mm, axis (0,0,-1), area 0.2mm2, adj f80,f82,f84,f89
  f84: cylinder r=0.75mm len=1.5mm, axis (0,0,-1), area 1.4mm2, adj f80,f83,f85,f86
  f85: plane 1.5x1.5mm, normal (0,0,-1), area 1.8mm2, adj f84
  f86: plane 0.46x0.4mm, normal (0,-1,0), area 0.1mm2, adj f80,f84,f89
  f87: cylinder r=0.75mm len=1.5mm, axis (0,0,-1), area 0.2mm2, adj f79,f80,f81,f89
  f88: cylinder r=0.75mm len=2.5mm, axis (0,0,-1), area 5.9mm2, adj f79
  f89: bspline ~2.65x2.48mm, area 11.7mm2, adj f79,f80,f81,f82,f83,f86,f87
  f90: cylinder r=1.5mm len=3.5mm, axis (0,0,1), area 33mm2, adj f10,f91
  f91: plane 3.3x3.3mm, normal (0,0,-1), area 2.5mm2, adj f90,f92,f99,f100,f101
  f92: bspline ~2.73x2.65mm, area 12.8mm2, adj f91,f93,f94,f95,f96,f98,f99,f101
  f93: cylinder r=0.75mm len=1.5mm, axis (0,0,-1), area 0.2mm2, adj f92,f94,f99,f101
  f94: cylinder r=0.75mm len=1.5mm, axis (0,0,-1), area 0.2mm2, adj f92,f93,f95,f101
  f95: cylinder r=0.75mm len=1.5mm, axis (0,0,-1), area 0.2mm2, adj f92,f94,f96,f101
  f96: cylinder r=0.75mm len=1.5mm, axis (0,0,-1), area 1.4mm2, adj f92,f95,f97,f98
  f97: plane 1.5x1.5mm, normal (0,0,-1), area 1.8mm2, adj f96
  f98: plane 0.46x0.4mm, normal (0,-1,0), area 0.1mm2, adj f92,f96,f101
  f99: cylinder r=0.75mm len=1.5mm, axis (0,0,-1), area 0.2mm2, adj f91,f92,f93,f101
  f100: cylinder r=0.75mm len=2.5mm, axis (0,0,-1), area 5.9mm2, adj f91
  f101: bspline ~2.65x2.48mm, area 11.7mm2, adj f91,f92,f93,f94,f95,f98,f99
  f102: cylinder r=0.75mm len=1.5mm, axis (0,0,-1), area -1.2mm2, adj f103
  f103: plane 4.5x4.5mm, normal (0,0,1), area 1.8mm2, adj f102
PLACE A t=(-30.78,12.23,63.7)mm fixed
PLACE B t=(94.02,12.23,56.7)mm fixed
PLACE C t=(94.02,12.23,57.2)mm fixed
PLACE D t=(69.67,27.93,65.7)mm fixed
MATE fastened C.f14 <-> B.f7  axis (0,0,-1) through (94.08,12.23,57.2)mm
MATE fastened C.f19 <-> D.f12  axis (0,0,-1) through (76.02,30.23,62.7)mm
MATE fastened B.f128 <-> A.f5  axis (0,0,1) through (-27.04,12.23,61.7)mm
